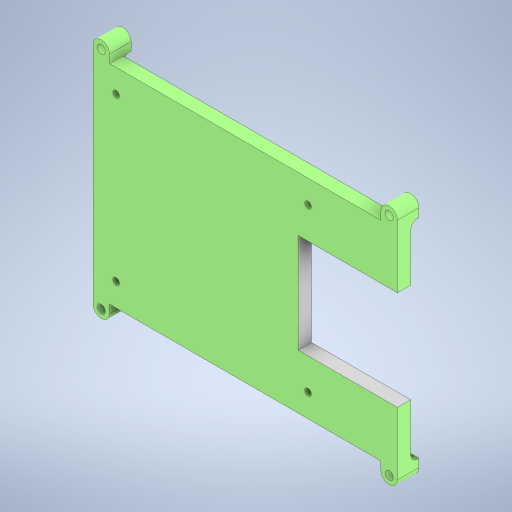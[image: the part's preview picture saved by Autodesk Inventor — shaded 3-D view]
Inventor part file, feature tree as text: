
AUTODESK INVENTOR PART (.ipt)
format: ipt  version: 2023.1 (Build 271208000, 208)  size: 343,040 bytes
history: native  units: mm
features: extrude x4, sketch x3, fillet x2, other x1
ambient origin geometry x8: Origin, YZ Plane, XZ Plane, XY Plane, X Axis, Y Axis, Z Axis, Center Point
bodies: Body1 (feature_tree)
feature tree (10):
  other  "솔리드1"
  sketch  "스케치1"
  extrude  "돌출1"  Depth=92.0mm
  extrude  "돌출3"  Depth=63.0mm
  extrude  "돌출4"  Depth=85.0mm
  fillet  "모깎기1"  Radius=56.0mm
  fillet  "모깎기2"  Radius=3.5mm
  extrude  "돌출5"  Depth=3.5mm
  sketch  "스케치3"
  sketch  "스케치4"
